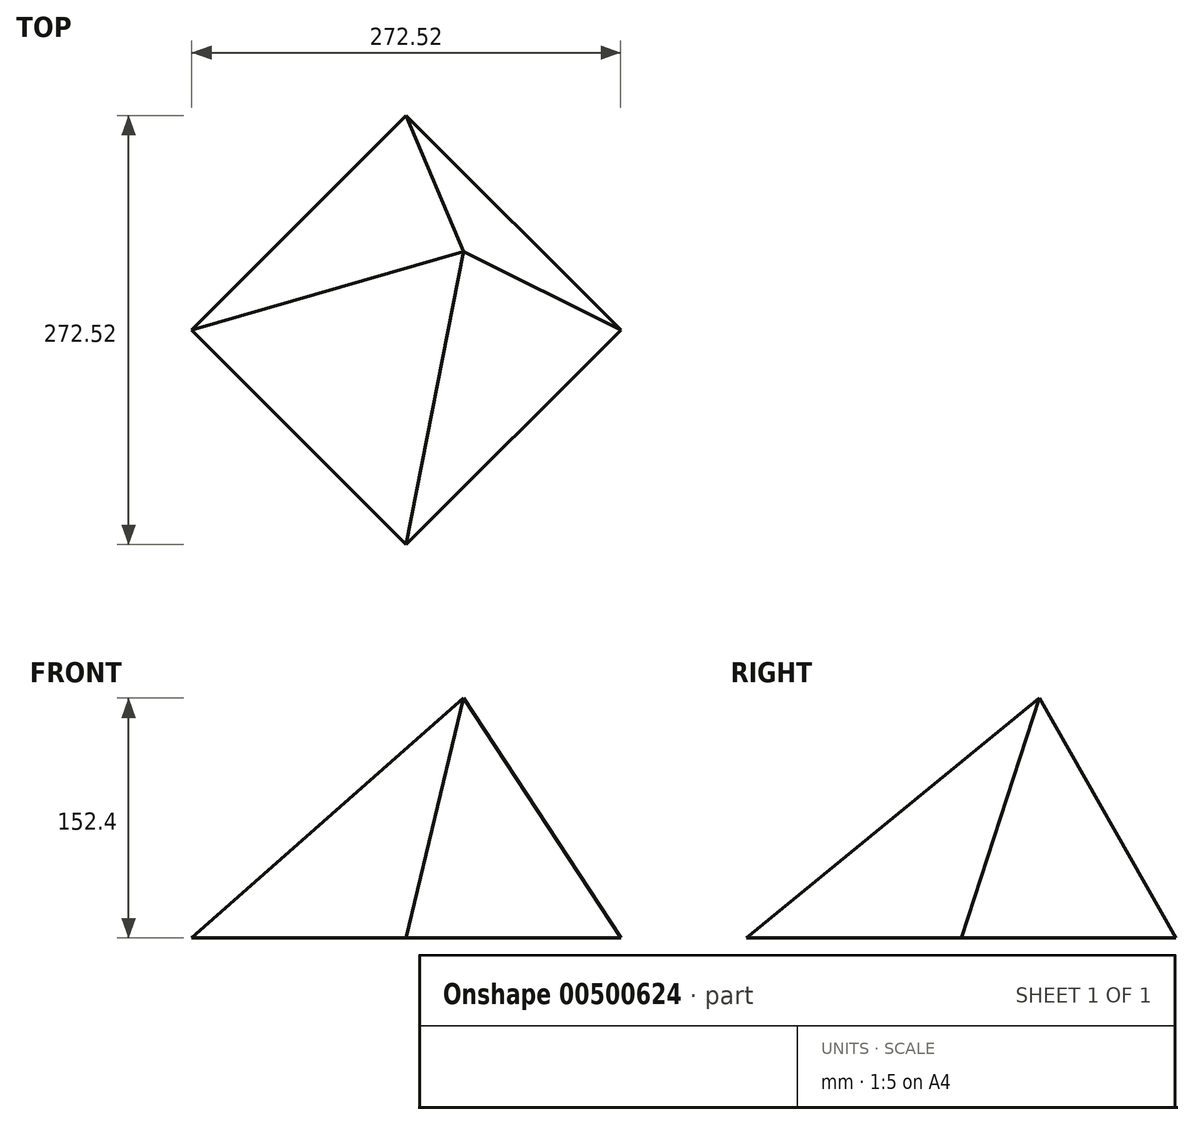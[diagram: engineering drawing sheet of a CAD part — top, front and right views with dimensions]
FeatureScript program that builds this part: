
annotation { "Feature Type Name" : "Feature", "Feature Type Description" : "" }
export const myFeature = defineFeature(function(context is Context, id is Id, definition is map)
    precondition{}
    {
        {
            var Q0;
            Q0=qCreatedBy(makeId("Top.planeOp"),FACE);
            var sketch = newSketch(context, id + "F0", { "sketchPlane" : qUnion([Q0])});
            skCircle(sketch, "E0.cCircle", {"center": v(0, 0) * mm, "radius": 136.26 * mm, "construction": true});
            skLineSegment(sketch, "E0.0", {"start": v(136.26, 0) * mm, "end": v(0, -136.26) * mm});
            skLineSegment(sketch, "E0.1", {"start": v(0, -136.26) * mm, "end": v(-136.26, 0) * mm});
            skLineSegment(sketch, "E0.2", {"start": v(-136.26, 0) * mm, "end": v(0, 136.26) * mm});
            skLineSegment(sketch, "E0.3", {"start": v(0, 136.26) * mm, "end": v(136.26, 0) * mm});
            skSolve(sketch);
        }
        {
            var Q0;
            Q0=qCreatedBy(makeId("Top.planeOp"),FACE);
            cPlane(context, id + "F1", {"entities" : qUnion([Q0]), "cplaneType" : CPlaneType.OFFSET, "offset" : 152.4 * mm, "width" : 152.4 * mm, "height" : 152.4 * mm});
        }
        {
            var Q0;
            Q0=qCreatedBy(id+"F1.planeOp",FACE);
            var sketch = newSketch(context, id + "F2", { "sketchPlane" : qUnion([Q0])});
            skPoint(sketch, "E1", {"position": v(36.43, 49.7) * mm});
            skSolve(sketch);
        }
        {
            var Q0;
            Q0=makeQuery(id+"F0.imprint","IMPRINT",FACE,{"disambiguationData":[TD([[makeQuery(id+"F0.imprint","IMPRINT",EDGE,{"derivedFrom":sQuery(id+"F0.wireOp",EDGE,"E0.0")}),-1.0]])]});
            var Q1;
            Q1=sQuery(id+"F2.wireOp",VERTEX,"E1");
            loft(context, id + "F3", {"sheetProfilesArray" : [{ "sheetProfileEntities" : qUnion([Q0]) }, { "sheetProfileEntities" : qUnion([Q1]) }]});
        }
    });
